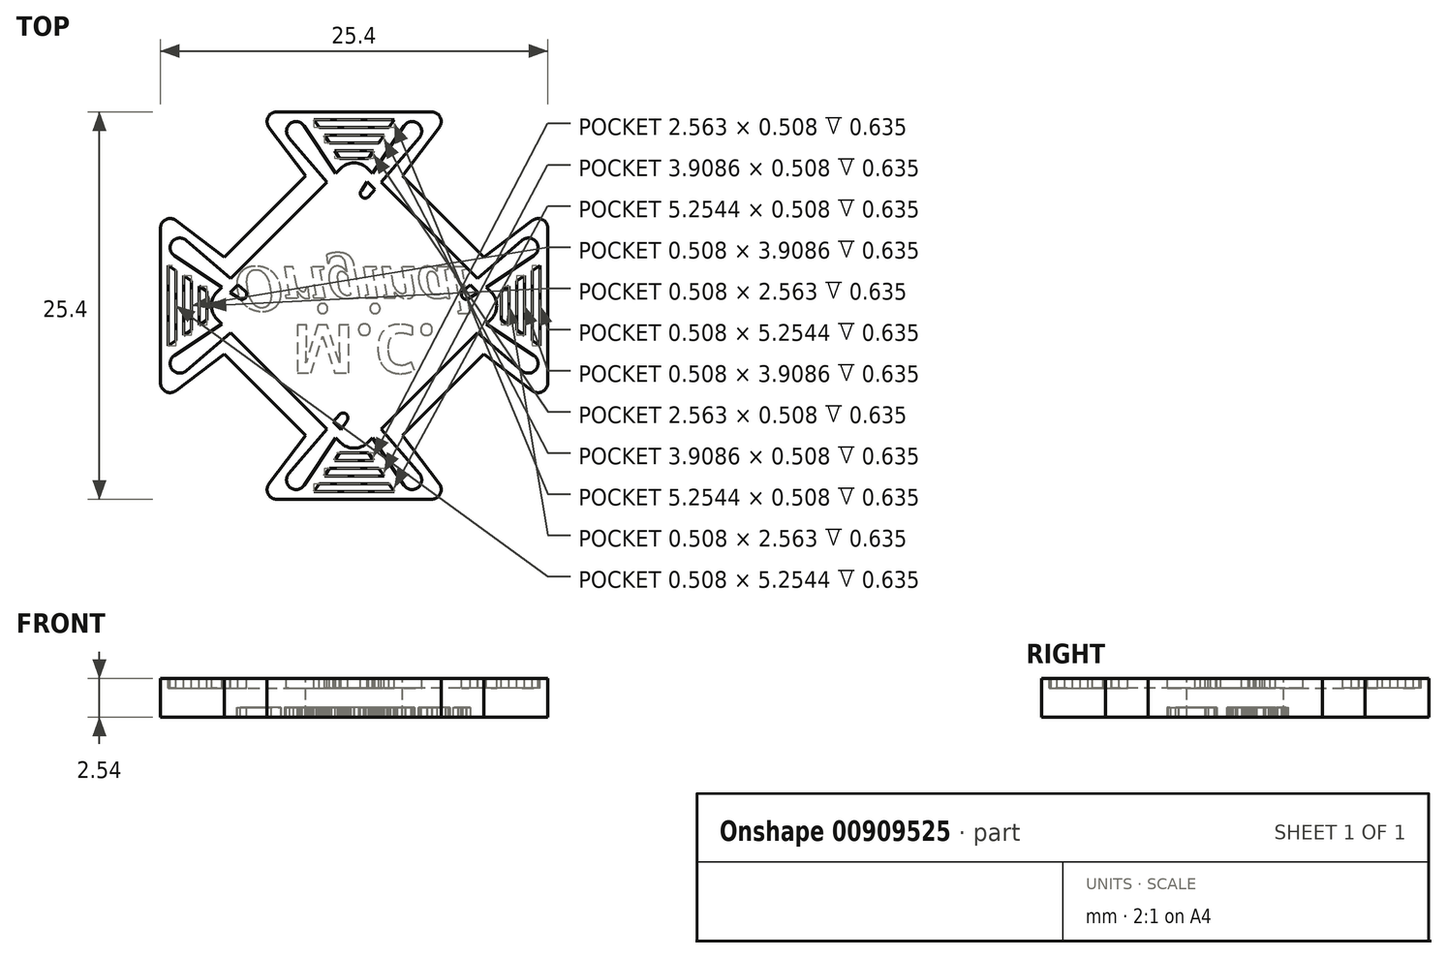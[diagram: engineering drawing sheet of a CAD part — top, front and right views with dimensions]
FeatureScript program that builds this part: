
annotation { "Feature Type Name" : "Feature", "Feature Type Description" : "" }
export const myFeature = defineFeature(function(context is Context, id is Id, definition is map)
    precondition{}
    {
        {
            var Q0;
            Q0=qCreatedBy(makeId("Top.planeOp"),FACE);
            var sketch = newSketch(context, id + "F0", { "sketchPlane" : qUnion([Q0])});
            skLineSegment(sketch, "E0", {"start": v(0, 24.37) * mm, "end": v(0, -22.03) * mm, "construction": true});
            skLineSegment(sketch, "E1", {"start": v(-24.6, 0) * mm, "end": v(22.72, 0) * mm, "construction": true});
            skLineSegment(sketch, "E2", {"start": v(0, 11.67) * mm, "end": v(-11.67, 0) * mm});
            skLineSegment(sketch, "E3.MirrorCS", {"start": v(0, 11.67) * mm, "end": v(11.67, 0) * mm});
            skLineSegment(sketch, "E4.MirrorCS", {"start": v(0, -11.67) * mm, "end": v(-11.67, 0) * mm});
            skLineSegment(sketch, "E5.MirrorCS", {"start": v(0, -11.67) * mm, "end": v(11.67, 0) * mm});
            skLineSegment(sketch, "E6", {"start": v(0, 12.7) * mm, "end": v(-6.35, 12.7) * mm});
            skLineSegment(sketch, "E7", {"start": v(-6.35, 12.7) * mm, "end": v(-3.17, 8.5) * mm});
            skPoint(sketch, "E7.endSnap0", {"position": v(-3.17, 12.7) * mm});
            skLineSegment(sketch, "E8.MirrorCS", {"start": v(0, 12.7) * mm, "end": v(6.35, 12.7) * mm});
            skLineSegment(sketch, "E9.MirrorCS", {"start": v(6.35, 12.7) * mm, "end": v(3.17, 8.5) * mm});
            skLineSegment(sketch, "E10.MirrorCS", {"start": v(6.35, -12.7) * mm, "end": v(3.17, -8.5) * mm});
            skLineSegment(sketch, "E11.MirrorCS", {"start": v(0, -12.7) * mm, "end": v(6.35, -12.7) * mm});
            skLineSegment(sketch, "E12.MirrorCS", {"start": v(0, -12.7) * mm, "end": v(-6.35, -12.7) * mm});
            skLineSegment(sketch, "E13.MirrorCS", {"start": v(-6.35, -12.7) * mm, "end": v(-3.17, -8.5) * mm});
            skLineSegment(sketch, "E14", {"start": v(0, 0) * mm, "end": v(5.84, -5.84) * mm, "construction": true});
            skLineSegment(sketch, "E15.MirrorCS", {"start": v(12.7, -6.35) * mm, "end": v(8.5, -3.18) * mm});
            skLineSegment(sketch, "E16.MirrorCS", {"start": v(12.7, 0) * mm, "end": v(12.7, -6.35) * mm});
            skLineSegment(sketch, "E17.MirrorCS", {"start": v(12.7, 0) * mm, "end": v(12.7, 6.35) * mm});
            skLineSegment(sketch, "E18.MirrorCS", {"start": v(12.7, 6.35) * mm, "end": v(8.5, 3.17) * mm});
            skLineSegment(sketch, "E19.MirrorCS", {"start": v(-12.7, 6.35) * mm, "end": v(-8.5, 3.17) * mm});
            skLineSegment(sketch, "E20.MirrorCS", {"start": v(-12.7, 0) * mm, "end": v(-12.7, 6.35) * mm});
            skLineSegment(sketch, "E21.MirrorCS", {"start": v(-12.7, 0) * mm, "end": v(-12.7, -6.35) * mm});
            skLineSegment(sketch, "E22.MirrorCS", {"start": v(-12.7, -6.35) * mm, "end": v(-8.5, -3.18) * mm});
            skSolve(sketch);
        }
        {
            var Q0;
            Q0=qSketchRegion(id+"F0",true);
            extrude(context, id + "F1", {"entities" : qUnion([Q0]), "oppositeDirection" : true, "depth" : 2.54 * mm, "offsetDistance" : 25.4 * mm});
        }
        {
            var Q0;
            Q0=makeQuery(id+"F1.opExtrude","SWEPT_EDGE",EDGE,{"disambiguationData":[OSD([sQuery(id+"F0.wireOp",EDGE,"E6"),sQuery(id+"F0.wireOp",EDGE,"E7")])]});
            var Q1;
            Q1=makeQuery(id+"F1.opExtrude","SWEPT_EDGE",EDGE,{"disambiguationData":[OSD([sQuery(id+"F0.wireOp",EDGE,"E19.MirrorCS"),sQuery(id+"F0.wireOp",EDGE,"E20.MirrorCS")])]});
            var Q2;
            Q2=makeQuery(id+"F1.opExtrude","SWEPT_EDGE",EDGE,{"disambiguationData":[OSD([sQuery(id+"F0.wireOp",EDGE,"E8.MirrorCS"),sQuery(id+"F0.wireOp",EDGE,"E9.MirrorCS")])]});
            var Q3;
            Q3=makeQuery(id+"F1.opExtrude","SWEPT_EDGE",EDGE,{"disambiguationData":[OSD([sQuery(id+"F0.wireOp",EDGE,"E17.MirrorCS"),sQuery(id+"F0.wireOp",EDGE,"E18.MirrorCS")])]});
            var Q4;
            Q4=makeQuery(id+"F1.opExtrude","SWEPT_EDGE",EDGE,{"disambiguationData":[OSD([sQuery(id+"F0.wireOp",EDGE,"E12.MirrorCS"),sQuery(id+"F0.wireOp",EDGE,"E13.MirrorCS")])]});
            var Q5;
            Q5=makeQuery(id+"F1.opExtrude","SWEPT_EDGE",EDGE,{"disambiguationData":[OSD([sQuery(id+"F0.wireOp",EDGE,"E21.MirrorCS"),sQuery(id+"F0.wireOp",EDGE,"E22.MirrorCS")])]});
            var Q6;
            Q6=makeQuery(id+"F1.opExtrude","SWEPT_EDGE",EDGE,{"disambiguationData":[OSD([sQuery(id+"F0.wireOp",EDGE,"E10.MirrorCS"),sQuery(id+"F0.wireOp",EDGE,"E11.MirrorCS")])]});
            var Q7;
            Q7=makeQuery(id+"F1.opExtrude","SWEPT_EDGE",EDGE,{"disambiguationData":[OSD([sQuery(id+"F0.wireOp",EDGE,"E15.MirrorCS"),sQuery(id+"F0.wireOp",EDGE,"E16.MirrorCS")])]});
            fillet(context, id + "F2", {"entities" : qUnion([Q0, Q1, Q2, Q3, Q4, Q5, Q6, Q7]), "radius" : 0.64 * mm, "tangentPropagation" : true, "allowEdgeOverflow" : false});
        }
        {
            var Q0;
            Q0=makeQuery(id+"F1.opExtrude","CAP_FACE",FACE,{"disambiguationData":[OSD([sQuery(id+"F0.wireOp",EDGE,"E2"),sQuery(id+"F0.wireOp",EDGE,"E3.MirrorCS"),sQuery(id+"F0.wireOp",EDGE,"E4.MirrorCS"),sQuery(id+"F0.wireOp",EDGE,"E5.MirrorCS"),sQuery(id+"F0.wireOp",EDGE,"E6"),sQuery(id+"F0.wireOp",EDGE,"E7"),sQuery(id+"F0.wireOp",EDGE,"E8.MirrorCS"),sQuery(id+"F0.wireOp",EDGE,"E9.MirrorCS"),sQuery(id+"F0.wireOp",EDGE,"E10.MirrorCS"),sQuery(id+"F0.wireOp",EDGE,"E11.MirrorCS"),sQuery(id+"F0.wireOp",EDGE,"E12.MirrorCS"),sQuery(id+"F0.wireOp",EDGE,"E13.MirrorCS"),sQuery(id+"F0.wireOp",EDGE,"E15.MirrorCS"),sQuery(id+"F0.wireOp",EDGE,"E16.MirrorCS"),sQuery(id+"F0.wireOp",EDGE,"E17.MirrorCS"),sQuery(id+"F0.wireOp",EDGE,"E18.MirrorCS"),sQuery(id+"F0.wireOp",EDGE,"E19.MirrorCS"),sQuery(id+"F0.wireOp",EDGE,"E20.MirrorCS"),sQuery(id+"F0.wireOp",EDGE,"E21.MirrorCS"),sQuery(id+"F0.wireOp",EDGE,"E22.MirrorCS")])],"isStart":true});
            var sketch = newSketch(context, id + "F3", { "sketchPlane" : qUnion([Q0])});
            skLineSegment(sketch, "E23", {"start": v(0, 16.4) * mm, "end": v(0, -16.14) * mm, "construction": true});
            skLineSegment(sketch, "E24", {"start": v(-8.98, 0.9) * mm, "end": v(-0.9, 8.98) * mm});
            skArc(sketch, "E25", {"start": v(0, 9.35) * mm, "mid": v(-0.49, 9.26) * mm, "end": v(-0.9, 8.98) * mm});
            skLineSegment(sketch, "E26", {"start": v(0, 0) * mm, "end": v(-13.8, 0) * mm, "construction": true});
            skLineSegment(sketch, "E27", {"start": v(0, 0) * mm, "end": v(-5.84, 5.84) * mm, "construction": true});
            skArc(sketch, "E28.MirrorCS", {"start": v(-9.35, 0) * mm, "mid": v(-9.26, 0.49) * mm, "end": v(-8.98, 0.9) * mm});
            skPoint(sketch, "E29.start.orphan", {"position": v(-9.88, 0) * mm});
            skArc(sketch, "E30.MirrorCS", {"start": v(-9.35, 0) * mm, "mid": v(-9.26, -0.49) * mm, "end": v(-8.98, -0.9) * mm});
            skLineSegment(sketch, "E31.MirrorCS", {"start": v(-8.98, -0.9) * mm, "end": v(-0.9, -8.98) * mm});
            skArc(sketch, "E32.MirrorCS", {"start": v(0, -9.35) * mm, "mid": v(-0.49, -9.26) * mm, "end": v(-0.9, -8.98) * mm});
            skArc(sketch, "E33.MirrorCS", {"start": v(0, 9.35) * mm, "mid": v(0.49, 9.26) * mm, "end": v(0.9, 8.98) * mm});
            skLineSegment(sketch, "E34.MirrorCS", {"start": v(8.98, 0.9) * mm, "end": v(0.9, 8.98) * mm});
            skArc(sketch, "E35.MirrorCS", {"start": v(9.35, 0) * mm, "mid": v(9.26, 0.49) * mm, "end": v(8.98, 0.9) * mm});
            skArc(sketch, "E36.MirrorCS", {"start": v(9.35, 0) * mm, "mid": v(9.26, -0.49) * mm, "end": v(8.98, -0.9) * mm});
            skLineSegment(sketch, "E37.MirrorCS", {"start": v(8.98, -0.9) * mm, "end": v(0.9, -8.98) * mm});
            skArc(sketch, "E38.MirrorCS", {"start": v(0, -9.35) * mm, "mid": v(0.49, -9.26) * mm, "end": v(0.9, -8.98) * mm});
            skLineSegment(sketch, "E39", {"start": v(-2.75, 10.05) * mm, "end": v(2.55, 3.03) * mm, "construction": true});
            skArc(sketch, "E40", {"start": v(-4.18, 11.94) * mm, "mid": v(-4.43, 11.5) * mm, "end": v(-4.28, 11.02) * mm});
            skArc(sketch, "E41", {"start": v(-0.96, 7.15) * mm, "mid": v(-0.76, 7.04) * mm, "end": v(-0.53, 7.1) * mm});
            skLineSegment(sketch, "E42", {"start": v(-4.28, 11.02) * mm, "end": v(-0.96, 7.15) * mm});
            skArc(sketch, "E43.MirrorCS", {"start": v(-0.46, 7.54) * mm, "mid": v(-0.4, 7.3) * mm, "end": v(-0.53, 7.1) * mm});
            skLineSegment(sketch, "E44.MirrorCS", {"start": v(-3.27, 11.78) * mm, "end": v(-0.46, 7.54) * mm});
            skArc(sketch, "E45.MirrorCS", {"start": v(-4.18, 11.94) * mm, "mid": v(-3.7, 12.06) * mm, "end": v(-3.27, 11.78) * mm});
            skArc(sketch, "E46.MirrorCS", {"start": v(4.18, 11.94) * mm, "mid": v(3.7, 12.06) * mm, "end": v(3.27, 11.78) * mm});
            skArc(sketch, "E47.MirrorCS", {"start": v(4.18, 11.94) * mm, "mid": v(4.43, 11.5) * mm, "end": v(4.28, 11.02) * mm});
            skLineSegment(sketch, "E48.MirrorCS", {"start": v(4.28, 11.02) * mm, "end": v(0.96, 7.15) * mm});
            skLineSegment(sketch, "E49.MirrorCS", {"start": v(3.27, 11.78) * mm, "end": v(0.46, 7.54) * mm});
            skArc(sketch, "E50.MirrorCS", {"start": v(0.96, 7.15) * mm, "mid": v(0.76, 7.04) * mm, "end": v(0.53, 7.1) * mm});
            skArc(sketch, "E51.MirrorCS", {"start": v(0.46, 7.54) * mm, "mid": v(0.4, 7.3) * mm, "end": v(0.53, 7.1) * mm});
            skArc(sketch, "E52.MirrorCS", {"start": v(-11.94, 4.18) * mm, "mid": v(-11.5, 4.43) * mm, "end": v(-11.02, 4.28) * mm});
            skArc(sketch, "E53.MirrorCS", {"start": v(-11.94, 4.18) * mm, "mid": v(-12.06, 3.7) * mm, "end": v(-11.78, 3.27) * mm});
            skLineSegment(sketch, "E54.MirrorCS", {"start": v(-11.02, 4.28) * mm, "end": v(-7.15, 0.96) * mm});
            skLineSegment(sketch, "E55.MirrorCS", {"start": v(-11.78, 3.27) * mm, "end": v(-7.54, 0.46) * mm});
            skArc(sketch, "E56.MirrorCS", {"start": v(-7.15, 0.96) * mm, "mid": v(-7.04, 0.76) * mm, "end": v(-7.1, 0.53) * mm});
            skArc(sketch, "E57.MirrorCS", {"start": v(-7.54, 0.46) * mm, "mid": v(-7.3, 0.4) * mm, "end": v(-7.1, 0.53) * mm});
            skArc(sketch, "E58.MirrorCS", {"start": v(-7.15, -0.96) * mm, "mid": v(-7.04, -0.76) * mm, "end": v(-7.1, -0.53) * mm});
            skArc(sketch, "E59.MirrorCS", {"start": v(-7.54, -0.46) * mm, "mid": v(-7.3, -0.4) * mm, "end": v(-7.1, -0.53) * mm});
            skLineSegment(sketch, "E60.MirrorCS", {"start": v(-11.78, -3.27) * mm, "end": v(-7.54, -0.46) * mm});
            skLineSegment(sketch, "E61.MirrorCS", {"start": v(-11.02, -4.28) * mm, "end": v(-7.15, -0.96) * mm});
            skArc(sketch, "E62.MirrorCS", {"start": v(-11.94, -4.18) * mm, "mid": v(-12.06, -3.7) * mm, "end": v(-11.78, -3.27) * mm});
            skArc(sketch, "E63.MirrorCS", {"start": v(-11.94, -4.18) * mm, "mid": v(-11.5, -4.43) * mm, "end": v(-11.02, -4.28) * mm});
            skArc(sketch, "E64.MirrorCS", {"start": v(11.94, 4.18) * mm, "mid": v(11.5, 4.43) * mm, "end": v(11.02, 4.28) * mm});
            skArc(sketch, "E65.MirrorCS", {"start": v(11.94, 4.18) * mm, "mid": v(12.06, 3.7) * mm, "end": v(11.78, 3.27) * mm});
            skLineSegment(sketch, "E66.MirrorCS", {"start": v(11.78, 3.27) * mm, "end": v(7.54, 0.46) * mm});
            skLineSegment(sketch, "E67.MirrorCS", {"start": v(11.02, 4.28) * mm, "end": v(7.15, 0.96) * mm});
            skArc(sketch, "E68.MirrorCS", {"start": v(11.94, -4.18) * mm, "mid": v(12.06, -3.7) * mm, "end": v(11.78, -3.27) * mm});
            skArc(sketch, "E69.MirrorCS", {"start": v(11.94, -4.18) * mm, "mid": v(11.5, -4.43) * mm, "end": v(11.02, -4.28) * mm});
            skLineSegment(sketch, "E70.MirrorCS", {"start": v(11.02, -4.28) * mm, "end": v(7.15, -0.96) * mm});
            skLineSegment(sketch, "E71.MirrorCS", {"start": v(11.78, -3.27) * mm, "end": v(7.54, -0.46) * mm});
            skArc(sketch, "E72.MirrorCS", {"start": v(7.54, -0.46) * mm, "mid": v(7.3, -0.4) * mm, "end": v(7.1, -0.53) * mm});
            skArc(sketch, "E73.MirrorCS", {"start": v(7.15, -0.96) * mm, "mid": v(7.04, -0.76) * mm, "end": v(7.1, -0.53) * mm});
            skArc(sketch, "E74.MirrorCS", {"start": v(7.54, 0.46) * mm, "mid": v(7.3, 0.4) * mm, "end": v(7.1, 0.53) * mm});
            skArc(sketch, "E75.MirrorCS", {"start": v(7.15, 0.96) * mm, "mid": v(7.04, 0.76) * mm, "end": v(7.1, 0.53) * mm});
            skArc(sketch, "E76.MirrorCS", {"start": v(-4.18, -11.94) * mm, "mid": v(-3.7, -12.06) * mm, "end": v(-3.27, -11.78) * mm});
            skArc(sketch, "E77.MirrorCS", {"start": v(-4.18, -11.94) * mm, "mid": v(-4.43, -11.5) * mm, "end": v(-4.28, -11.02) * mm});
            skLineSegment(sketch, "E78.MirrorCS", {"start": v(-4.28, -11.02) * mm, "end": v(-0.96, -7.15) * mm});
            skLineSegment(sketch, "E79.MirrorCS", {"start": v(-3.27, -11.78) * mm, "end": v(-0.46, -7.54) * mm});
            skArc(sketch, "E80.MirrorCS", {"start": v(-0.96, -7.15) * mm, "mid": v(-0.76, -7.04) * mm, "end": v(-0.53, -7.1) * mm});
            skArc(sketch, "E81.MirrorCS", {"start": v(-0.46, -7.54) * mm, "mid": v(-0.4, -7.3) * mm, "end": v(-0.53, -7.1) * mm});
            skArc(sketch, "E82.MirrorCS", {"start": v(0.96, -7.15) * mm, "mid": v(0.76, -7.04) * mm, "end": v(0.53, -7.1) * mm});
            skArc(sketch, "E83.MirrorCS", {"start": v(0.46, -7.54) * mm, "mid": v(0.4, -7.3) * mm, "end": v(0.53, -7.1) * mm});
            skLineSegment(sketch, "E84.MirrorCS", {"start": v(3.27, -11.78) * mm, "end": v(0.46, -7.54) * mm});
            skLineSegment(sketch, "E85.MirrorCS", {"start": v(4.28, -11.02) * mm, "end": v(0.96, -7.15) * mm});
            skArc(sketch, "E86.MirrorCS", {"start": v(4.18, -11.94) * mm, "mid": v(3.7, -12.06) * mm, "end": v(3.27, -11.78) * mm});
            skArc(sketch, "E87.MirrorCS", {"start": v(4.18, -11.94) * mm, "mid": v(4.43, -11.5) * mm, "end": v(4.28, -11.02) * mm});
            skLineSegment(sketch, "E88.0", {"start": v(-8.53, 0.45) * mm, "end": v(-0.45, 8.53) * mm});
            skLineSegment(sketch, "E89.0", {"start": v(8.53, 0.45) * mm, "end": v(0.45, 8.53) * mm});
            skLineSegment(sketch, "E90.0", {"start": v(8.53, -0.45) * mm, "end": v(0.45, -8.53) * mm});
            skLineSegment(sketch, "E91.0", {"start": v(-8.53, -0.45) * mm, "end": v(-0.45, -8.53) * mm});
            skArc(sketch, "E92", {"start": v(0.45, 8.53) * mm, "mid": v(0, 8.72) * mm, "end": v(-0.45, 8.53) * mm});
            skPoint(sketch, "E93.end.orphan", {"position": v(0, 8.98) * mm});
            skPoint(sketch, "E94.MirrorCS.start.orphan", {"position": v(0.45, 8.53) * mm});
            skArc(sketch, "E95.MirrorCS", {"start": v(-8.53, -0.45) * mm, "mid": v(-8.72, 0) * mm, "end": v(-8.53, 0.45) * mm});
            skArc(sketch, "E96.MirrorCS", {"start": v(0.45, -8.53) * mm, "mid": v(0, -8.72) * mm, "end": v(-0.45, -8.53) * mm});
            skArc(sketch, "E97.MirrorCS", {"start": v(8.53, -0.45) * mm, "mid": v(8.72, 0) * mm, "end": v(8.53, 0.45) * mm});
            skSolve(sketch);
        }
        {
            var Q0;
            Q0=qSketchRegion(id+"F3",true);
            var Q1;
            {var subQ0=sQuery(id+"F3.wireOp",EDGE,"E80.MirrorCS");Q1=makeQuery(id+"F3.imprint","IMPRINT",FACE,{"disambiguationData":[TD([[makeQuery(id+"F3.imprint","IMPRINT",EDGE,{"derivedFrom":subQ0}),-1.0]])]});}
            var Q2;
            {var subQ1=sQuery(id+"F3.wireOp",EDGE,"E82.MirrorCS");Q2=makeQuery(id+"F3.imprint","IMPRINT",FACE,{"disambiguationData":[TD([[makeQuery(id+"F3.imprint","IMPRINT",EDGE,{"derivedFrom":subQ1}),1.0]])]});}
            var Q3;
            {var subQ0=sQuery(id+"F3.wireOp",EDGE,"E74.MirrorCS");Q3=makeQuery(id+"F3.imprint","IMPRINT",FACE,{"disambiguationData":[TD([[makeQuery(id+"F3.imprint","IMPRINT",EDGE,{"derivedFrom":subQ0}),-1.0]])]});}
            var Q4;
            {var subQ0=sQuery(id+"F3.wireOp",EDGE,"E50.MirrorCS");Q4=makeQuery(id+"F3.imprint","IMPRINT",FACE,{"disambiguationData":[TD([[makeQuery(id+"F3.imprint","IMPRINT",EDGE,{"derivedFrom":subQ0}),-1.0]])]});}
            var Q5;
            {var subQ1=sQuery(id+"F3.wireOp",EDGE,"E41");Q5=makeQuery(id+"F3.imprint","IMPRINT",FACE,{"disambiguationData":[TD([[makeQuery(id+"F3.imprint","IMPRINT",EDGE,{"derivedFrom":subQ1}),1.0]])]});}
            var Q6;
            {var subQ0=sQuery(id+"F3.wireOp",EDGE,"E56.MirrorCS");Q6=makeQuery(id+"F3.imprint","IMPRINT",FACE,{"disambiguationData":[TD([[makeQuery(id+"F3.imprint","IMPRINT",EDGE,{"derivedFrom":subQ0}),-1.0]])]});}
            var Q7;
            {var subQ4=sQuery(id+"F3.wireOp",EDGE,"E58.MirrorCS");Q7=makeQuery(id+"F3.imprint","IMPRINT",FACE,{"disambiguationData":[TD([[makeQuery(id+"F3.imprint","IMPRINT",EDGE,{"derivedFrom":subQ4}),1.0]])]});}
            var Q8;
            {var subQ0=sQuery(id+"F3.wireOp",EDGE,"E72.MirrorCS");Q8=makeQuery(id+"F3.imprint","IMPRINT",FACE,{"disambiguationData":[TD([[makeQuery(id+"F3.imprint","IMPRINT",EDGE,{"derivedFrom":subQ0}),1.0]])]});}
            extrude(context, id + "F4", {"entities" : qUnion([Q0, Q1, Q2, Q3, Q4, Q5, Q6, Q7, Q8]), "operationType" : NewBodyOperationType.REMOVE, "oppositeDirection" : true, "depth" : 0.64 * mm, "offsetDistance" : 25.4 * mm});
        }
        {
            var Q0;
            {var subQ29=sQuery(id+"F0.wireOp",EDGE,"E22.MirrorCS");var subQ30=sQuery(id+"F0.wireOp",EDGE,"E21.MirrorCS");var subQ31=sQuery(id+"F0.wireOp",EDGE,"E17.MirrorCS");var subQ32=sQuery(id+"F0.wireOp",EDGE,"E16.MirrorCS");var subQ33=sQuery(id+"F0.wireOp",EDGE,"E20.MirrorCS");var subQ34=sQuery(id+"F0.wireOp",EDGE,"E19.MirrorCS");var subQ35=sQuery(id+"F0.wireOp",EDGE,"E15.MirrorCS");var subQ37=sQuery(id+"F0.wireOp",EDGE,"E12.MirrorCS");var subQ38=sQuery(id+"F0.wireOp",EDGE,"E11.MirrorCS");var subQ39=sQuery(id+"F0.wireOp",EDGE,"E9.MirrorCS");var subQ40=sQuery(id+"F0.wireOp",EDGE,"E8.MirrorCS");var subQ41=sQuery(id+"F0.wireOp",EDGE,"E7");var subQ44=sQuery(id+"F0.wireOp",EDGE,"E10.MirrorCS");var subQ45=sQuery(id+"F0.wireOp",EDGE,"E13.MirrorCS");var subQ46=sQuery(id+"F0.wireOp",EDGE,"E6");var subQ52=sQuery(id+"F0.wireOp",EDGE,"E18.MirrorCS");var subQ53=sQuery(id+"F0.wireOp",EDGE,"E2");var subQ58=sQuery(id+"F0.wireOp",EDGE,"E5.MirrorCS");var subQ59=sQuery(id+"F0.wireOp",EDGE,"E3.MirrorCS");var subQ60=sQuery(id+"F0.wireOp",EDGE,"E4.MirrorCS");Q0=makeQuery(id+"F4.boolean.opBoolean","SPLIT",FACE,{"disambiguationData":[TD([makeQuery(id+"F1.opExtrude","SWEPT_FACE",FACE,{"disambiguationData":[OSD([subQ53])]})])],"derivedFrom":makeQuery(id+"F1.opExtrude","CAP_FACE",FACE,{"disambiguationData":[OSD([subQ53,subQ59,subQ60,subQ58,subQ46,subQ41,subQ40,subQ39,subQ44,subQ38,subQ37,subQ45,subQ35,subQ32,subQ31,subQ52,subQ34,subQ33,subQ30,subQ29])],"isStart":true})});}
            var sketch = newSketch(context, id + "F5", { "sketchPlane" : qUnion([Q0])});
            skLineSegment(sketch, "E98", {"start": v(0, 15.67) * mm, "end": v(0, -18.97) * mm, "construction": true});
            skLineSegment(sketch, "E99", {"start": v(-16.91, 0) * mm, "end": v(16.57, 0) * mm, "construction": true});
            skLineSegment(sketch, "E100", {"start": v(-12.2, 2.63) * mm, "end": v(-12.2, 0) * mm});
            skLineSegment(sketch, "E101", {"start": v(-12.2, 2.63) * mm, "end": v(-8.22, 0) * mm, "construction": true});
            skLineSegment(sketch, "E102", {"start": v(-11.18, 1.95) * mm, "end": v(-11.18, 0) * mm});
            skLineSegment(sketch, "E103", {"start": v(-10.16, 1.28) * mm, "end": v(-10.16, 0) * mm});
            skLineSegment(sketch, "E104.0", {"start": v(-11.68, 2.3) * mm, "end": v(-11.68, 0) * mm});
            skLineSegment(sketch, "E105.0", {"start": v(-10.67, 1.62) * mm, "end": v(-10.67, 0) * mm});
            skLineSegment(sketch, "E106.0", {"start": v(-9.65, 0.95) * mm, "end": v(-9.65, 0) * mm});
            skLineSegment(sketch, "E107", {"start": v(-12.2, 2.63) * mm, "end": v(-11.68, 2.3) * mm});
            skLineSegment(sketch, "E108", {"start": v(-11.18, 1.95) * mm, "end": v(-10.67, 1.62) * mm});
            skLineSegment(sketch, "E109", {"start": v(-10.16, 1.28) * mm, "end": v(-9.65, 0.95) * mm});
            skLineSegment(sketch, "E110.MirrorCS", {"start": v(-12.2, -2.63) * mm, "end": v(-12.2, 0) * mm});
            skLineSegment(sketch, "E111.MirrorCS", {"start": v(-11.68, -2.3) * mm, "end": v(-11.68, 0) * mm});
            skLineSegment(sketch, "E112.MirrorCS", {"start": v(-11.18, -1.95) * mm, "end": v(-11.18, 0) * mm});
            skLineSegment(sketch, "E113.MirrorCS", {"start": v(-10.67, -1.62) * mm, "end": v(-10.67, 0) * mm});
            skLineSegment(sketch, "E114.MirrorCS", {"start": v(-10.16, -1.28) * mm, "end": v(-10.16, 0) * mm});
            skLineSegment(sketch, "E115.MirrorCS", {"start": v(-9.65, -0.95) * mm, "end": v(-9.65, 0) * mm});
            skLineSegment(sketch, "E116.MirrorCS", {"start": v(-10.16, -1.28) * mm, "end": v(-9.65, -0.95) * mm});
            skLineSegment(sketch, "E117.MirrorCS", {"start": v(-11.18, -1.95) * mm, "end": v(-10.67, -1.62) * mm});
            skLineSegment(sketch, "E118.MirrorCS", {"start": v(-12.2, -2.63) * mm, "end": v(-11.68, -2.3) * mm});
            skLineSegment(sketch, "E119.MirrorCS", {"start": v(12.2, 2.63) * mm, "end": v(11.68, 2.3) * mm});
            skLineSegment(sketch, "E120.MirrorCS", {"start": v(11.18, 1.95) * mm, "end": v(10.67, 1.62) * mm});
            skLineSegment(sketch, "E121.MirrorCS", {"start": v(10.16, 1.28) * mm, "end": v(9.65, 0.95) * mm});
            skLineSegment(sketch, "E122.MirrorCS", {"start": v(10.16, -1.28) * mm, "end": v(9.65, -0.95) * mm});
            skLineSegment(sketch, "E123.MirrorCS", {"start": v(11.18, -1.95) * mm, "end": v(10.67, -1.62) * mm});
            skLineSegment(sketch, "E124.MirrorCS", {"start": v(12.2, -2.63) * mm, "end": v(11.68, -2.3) * mm});
            skLineSegment(sketch, "E125.MirrorCS", {"start": v(12.2, -2.63) * mm, "end": v(12.2, 0) * mm});
            skLineSegment(sketch, "E126.MirrorCS", {"start": v(11.68, -2.3) * mm, "end": v(11.68, 0) * mm});
            skLineSegment(sketch, "E127.MirrorCS", {"start": v(11.18, -1.95) * mm, "end": v(11.18, 0) * mm});
            skLineSegment(sketch, "E128.MirrorCS", {"start": v(10.67, -1.62) * mm, "end": v(10.67, 0) * mm});
            skLineSegment(sketch, "E129.MirrorCS", {"start": v(10.16, -1.28) * mm, "end": v(10.16, 0) * mm});
            skLineSegment(sketch, "E130.MirrorCS", {"start": v(9.65, -0.95) * mm, "end": v(9.65, 0) * mm});
            skLineSegment(sketch, "E131.MirrorCS", {"start": v(9.65, 0.95) * mm, "end": v(9.65, 0) * mm});
            skLineSegment(sketch, "E132.MirrorCS", {"start": v(10.16, 1.28) * mm, "end": v(10.16, 0) * mm});
            skLineSegment(sketch, "E133.MirrorCS", {"start": v(10.67, 1.62) * mm, "end": v(10.67, 0) * mm});
            skLineSegment(sketch, "E134.MirrorCS", {"start": v(11.18, 1.95) * mm, "end": v(11.18, 0) * mm});
            skLineSegment(sketch, "E135.MirrorCS", {"start": v(11.68, 2.3) * mm, "end": v(11.68, 0) * mm});
            skLineSegment(sketch, "E136.MirrorCS", {"start": v(12.2, 2.63) * mm, "end": v(12.2, 0) * mm});
            skLineSegment(sketch, "E137", {"start": v(0, 0) * mm, "end": v(-5.84, 5.84) * mm, "construction": true});
            skLineSegment(sketch, "E138.MirrorCS", {"start": v(-2.63, 12.2) * mm, "end": v(-2.3, 11.68) * mm});
            skLineSegment(sketch, "E139.MirrorCS", {"start": v(-1.95, 11.18) * mm, "end": v(-1.62, 10.67) * mm});
            skLineSegment(sketch, "E140.MirrorCS", {"start": v(-1.28, 10.16) * mm, "end": v(-0.95, 9.65) * mm});
            skLineSegment(sketch, "E141.MirrorCS", {"start": v(1.28, 10.16) * mm, "end": v(0.95, 9.65) * mm});
            skLineSegment(sketch, "E142.MirrorCS", {"start": v(1.95, 11.18) * mm, "end": v(1.62, 10.67) * mm});
            skLineSegment(sketch, "E143.MirrorCS", {"start": v(2.63, 12.2) * mm, "end": v(2.3, 11.68) * mm});
            skLineSegment(sketch, "E144.MirrorCS", {"start": v(2.63, 12.2) * mm, "end": v(0, 12.2) * mm});
            skLineSegment(sketch, "E145.MirrorCS", {"start": v(2.3, 11.68) * mm, "end": v(0, 11.68) * mm});
            skLineSegment(sketch, "E146.MirrorCS", {"start": v(1.95, 11.18) * mm, "end": v(0, 11.18) * mm});
            skLineSegment(sketch, "E147.MirrorCS", {"start": v(1.62, 10.67) * mm, "end": v(0, 10.67) * mm});
            skLineSegment(sketch, "E148.MirrorCS", {"start": v(1.28, 10.16) * mm, "end": v(0, 10.16) * mm});
            skLineSegment(sketch, "E149.MirrorCS", {"start": v(0.95, 9.65) * mm, "end": v(0, 9.65) * mm});
            skLineSegment(sketch, "E150.MirrorCS", {"start": v(-0.95, 9.65) * mm, "end": v(0, 9.65) * mm});
            skLineSegment(sketch, "E151.MirrorCS", {"start": v(-1.28, 10.16) * mm, "end": v(0, 10.16) * mm});
            skLineSegment(sketch, "E152.MirrorCS", {"start": v(-1.62, 10.67) * mm, "end": v(0, 10.67) * mm});
            skLineSegment(sketch, "E153.MirrorCS", {"start": v(-1.95, 11.18) * mm, "end": v(0, 11.18) * mm});
            skLineSegment(sketch, "E154.MirrorCS", {"start": v(-2.3, 11.68) * mm, "end": v(0, 11.68) * mm});
            skLineSegment(sketch, "E155.MirrorCS", {"start": v(-2.63, 12.2) * mm, "end": v(0, 12.2) * mm});
            skLineSegment(sketch, "E156.MirrorCS", {"start": v(2.63, -12.2) * mm, "end": v(2.3, -11.68) * mm});
            skLineSegment(sketch, "E157.MirrorCS", {"start": v(1.95, -11.18) * mm, "end": v(1.62, -10.67) * mm});
            skLineSegment(sketch, "E158.MirrorCS", {"start": v(1.28, -10.16) * mm, "end": v(0.95, -9.65) * mm});
            skLineSegment(sketch, "E159.MirrorCS", {"start": v(-1.28, -10.16) * mm, "end": v(-0.95, -9.65) * mm});
            skLineSegment(sketch, "E160.MirrorCS", {"start": v(-1.95, -11.18) * mm, "end": v(-1.62, -10.67) * mm});
            skLineSegment(sketch, "E161.MirrorCS", {"start": v(-2.63, -12.2) * mm, "end": v(-2.3, -11.68) * mm});
            skLineSegment(sketch, "E162.MirrorCS", {"start": v(-2.63, -12.2) * mm, "end": v(0, -12.2) * mm});
            skLineSegment(sketch, "E163.MirrorCS", {"start": v(-2.3, -11.68) * mm, "end": v(0, -11.68) * mm});
            skLineSegment(sketch, "E164.MirrorCS", {"start": v(2.3, -11.68) * mm, "end": v(0, -11.68) * mm});
            skLineSegment(sketch, "E165.MirrorCS", {"start": v(2.63, -12.2) * mm, "end": v(0, -12.2) * mm});
            skLineSegment(sketch, "E166.MirrorCS", {"start": v(1.95, -11.18) * mm, "end": v(0, -11.18) * mm});
            skLineSegment(sketch, "E167.MirrorCS", {"start": v(-1.95, -11.18) * mm, "end": v(0, -11.18) * mm});
            skLineSegment(sketch, "E168.MirrorCS", {"start": v(-1.62, -10.67) * mm, "end": v(0, -10.67) * mm});
            skLineSegment(sketch, "E169.MirrorCS", {"start": v(1.62, -10.67) * mm, "end": v(0, -10.67) * mm});
            skLineSegment(sketch, "E170.MirrorCS", {"start": v(1.28, -10.16) * mm, "end": v(0, -10.16) * mm});
            skLineSegment(sketch, "E171.MirrorCS", {"start": v(-1.28, -10.16) * mm, "end": v(0, -10.16) * mm});
            skLineSegment(sketch, "E172.MirrorCS", {"start": v(-0.95, -9.65) * mm, "end": v(0, -9.65) * mm});
            skLineSegment(sketch, "E173.MirrorCS", {"start": v(0.95, -9.65) * mm, "end": v(0, -9.65) * mm});
            skSolve(sketch);
        }
        {
            var Q0;
            Q0=qSketchRegion(id+"F5",true);
            extrude(context, id + "F6", {"entities" : qUnion([Q0]), "operationType" : NewBodyOperationType.REMOVE, "oppositeDirection" : true, "depth" : 0.64 * mm, "offsetDistance" : 25.4 * mm});
        }
        {
            var Q0;
            Q0=makeQuery(id+"F1.opExtrude","CAP_FACE",FACE,{"disambiguationData":[OSD([sQuery(id+"F0.wireOp",EDGE,"E2"),sQuery(id+"F0.wireOp",EDGE,"E3.MirrorCS"),sQuery(id+"F0.wireOp",EDGE,"E4.MirrorCS"),sQuery(id+"F0.wireOp",EDGE,"E5.MirrorCS"),sQuery(id+"F0.wireOp",EDGE,"E6"),sQuery(id+"F0.wireOp",EDGE,"E7"),sQuery(id+"F0.wireOp",EDGE,"E8.MirrorCS"),sQuery(id+"F0.wireOp",EDGE,"E9.MirrorCS"),sQuery(id+"F0.wireOp",EDGE,"E10.MirrorCS"),sQuery(id+"F0.wireOp",EDGE,"E11.MirrorCS"),sQuery(id+"F0.wireOp",EDGE,"E12.MirrorCS"),sQuery(id+"F0.wireOp",EDGE,"E13.MirrorCS"),sQuery(id+"F0.wireOp",EDGE,"E15.MirrorCS"),sQuery(id+"F0.wireOp",EDGE,"E16.MirrorCS"),sQuery(id+"F0.wireOp",EDGE,"E17.MirrorCS"),sQuery(id+"F0.wireOp",EDGE,"E18.MirrorCS"),sQuery(id+"F0.wireOp",EDGE,"E19.MirrorCS"),sQuery(id+"F0.wireOp",EDGE,"E20.MirrorCS"),sQuery(id+"F0.wireOp",EDGE,"E21.MirrorCS"),sQuery(id+"F0.wireOp",EDGE,"E22.MirrorCS")])],"isStart":false});
            var sketch = newSketch(context, id + "F7", { "sketchPlane" : qUnion([Q0])});
            skText(sketch, "E174", { "text": "Original", "fontName": "Tinos-BoldItalic.ttf"});
            skLineSegment(sketch, "E175", {"start": v(0, 12.7) * mm, "end": v(0, -12.7) * mm});
            skText(sketch, "E176", { "text": "M.C.", "fontName": "OpenSans-Bold.ttf"});
            const initialGuessF7  = {"E174": [-0.00785, -0.00254, 1, 0, 0.00318], "E176": [-0.00412, 0.00127, 1, 0, 0.00318]};
            skSetInitialGuess(sketch, initialGuessF7);
            skSolve(sketch);
        }
        {
            var Q0;
            Q0=qSketchRegion(id+"F7",true);
            extrude(context, id + "F8", {"entities" : qUnion([Q0]), "operationType" : NewBodyOperationType.REMOVE, "oppositeDirection" : true, "depth" : 0.64 * mm, "offsetDistance" : 25.4 * mm});
        }
    });
